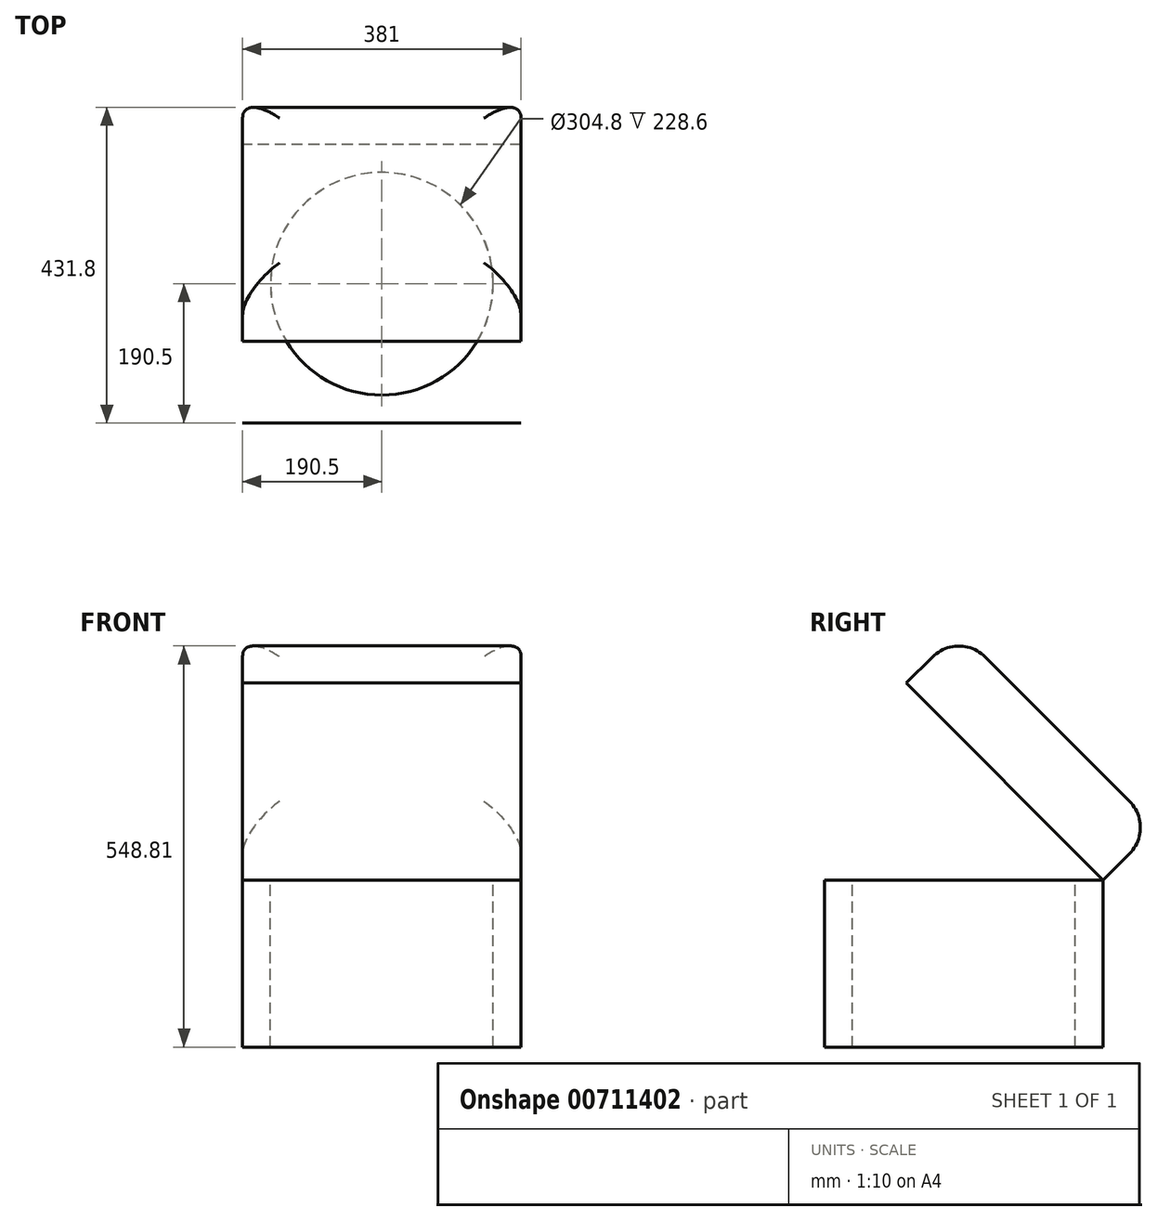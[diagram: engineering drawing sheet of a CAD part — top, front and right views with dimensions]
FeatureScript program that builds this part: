
annotation { "Feature Type Name" : "Feature", "Feature Type Description" : "" }
export const myFeature = defineFeature(function(context is Context, id is Id, definition is map)
    precondition{}
    {
        {
            var Q0;
            Q0=qCreatedBy(makeId("Top.planeOp"),FACE);
            var sketch = newSketch(context, id + "F0", { "sketchPlane" : qUnion([Q0])});
            skLineSegment(sketch, "E0.bottom", {"start": v(190.5, -190.5) * mm, "end": v(-190.5, -190.5) * mm});
            skLineSegment(sketch, "E0.top", {"start": v(190.5, 190.5) * mm, "end": v(-190.5, 190.5) * mm});
            skLineSegment(sketch, "E0.left", {"start": v(190.5, -190.5) * mm, "end": v(190.5, 190.5) * mm});
            skLineSegment(sketch, "E0.right", {"start": v(-190.5, -190.5) * mm, "end": v(-190.5, 190.5) * mm});
            skLineSegment(sketch, "E1", {"start": v(-190.5, 190.5) * mm, "end": v(190.5, -190.5) * mm, "construction": true});
            skSolve(sketch);
        }
        {
            var Q0;
            Q0=makeQuery(id+"F0.imprint","IMPRINT",FACE,{"disambiguationData":[TD([[makeQuery(id+"F0.imprint","IMPRINT",EDGE,{"derivedFrom":sQuery(id+"F0.wireOp",EDGE,"E0.bottom")}),-1.0]])]});
            extrude(context, id + "F1", {"entities" : qUnion([Q0]), "oppositeDirection" : true, "depth" : 228.6 * mm, "offsetDistance" : 25.4 * mm});
        }
        {
            var Q0;
            Q0=makeQuery(id+"F1.opExtrude","CAP_FACE",FACE,{"disambiguationData":[OSD([sQuery(id+"F0.wireOp",EDGE,"E0.bottom"),sQuery(id+"F0.wireOp",EDGE,"E0.top"),sQuery(id+"F0.wireOp",EDGE,"E0.left"),sQuery(id+"F0.wireOp",EDGE,"E0.right")])],"isStart":true});
            var Q1;
            Q1=makeQuery(id+"F1.opExtrude","CAP_EDGE",EDGE,{"disambiguationData":[OSD([sQuery(id+"F0.wireOp",EDGE,"E0.top")])],"isStart":true});
            cPlane(context, id + "F2", {"entities" : qUnion([Q0, Q1]), "cplaneType" : CPlaneType.LINE_ANGLE, "offset" : 25.4 * mm, "angle" : 45 * degree, "width" : 152.4 * mm, "height" : 152.4 * mm});
        }
        {
            var Q0;
            Q0=qCreatedBy(makeId("Right.planeOp"),FACE);
            var sketch = newSketch(context, id + "F3", { "sketchPlane" : qUnion([Q0])});
            skLineSegment(sketch, "E2.0", {"start": v(-190.5, 0) * mm, "end": v(190.5, 0) * mm, "construction": true});
            skLineSegment(sketch, "E3", {"start": v(190.5, 0) * mm, "end": v(-78.9, 269.4) * mm});
            skLineSegment(sketch, "E4", {"start": v(-78.9, 269.4) * mm, "end": v(-7.07, 341.25) * mm});
            skLineSegment(sketch, "E5", {"start": v(-7.07, 341.25) * mm, "end": v(262.34, 71.84) * mm});
            skLineSegment(sketch, "E6", {"start": v(262.34, 71.84) * mm, "end": v(190.5, 0) * mm});
            skSolve(sketch);
        }
        {
            var Q0;
            Q0=makeQuery(id+"F3.imprint","IMPRINT",FACE,{"disambiguationData":[TD([[makeQuery(id+"F3.imprint","IMPRINT",EDGE,{"derivedFrom":sQuery(id+"F3.wireOp",EDGE,"E3")}),-1.0]])]});
            extrude(context, id + "F4", {"entities" : qUnion([Q0]), "endBound" : BoundingType.SYMMETRIC, "depth" : 381 * mm, "offsetDistance" : 25.4 * mm});
        }
        {
            var Q0;
            Q0=makeQuery(id+"F4.opExtrude","SWEPT_FACE",FACE,{"disambiguationData":[OSD([sQuery(id+"F3.wireOp",EDGE,"E5")])]});
            fillet(context, id + "F5", {"entities" : qUnion([Q0]), "radius" : 50.8 * mm, "tangentPropagation" : true, "allowEdgeOverflow" : false});
        }
        {
            var Q0;
            Q0=makeQuery(id+"F1.opExtrude","CAP_FACE",FACE,{"disambiguationData":[OSD([sQuery(id+"F0.wireOp",EDGE,"E0.bottom"),sQuery(id+"F0.wireOp",EDGE,"E0.top"),sQuery(id+"F0.wireOp",EDGE,"E0.left"),sQuery(id+"F0.wireOp",EDGE,"E0.right")])],"isStart":true});
            var sketch = newSketch(context, id + "F6", { "sketchPlane" : qUnion([Q0])});
            skCircle(sketch, "E7", {"center": v(0, 0) * mm, "radius": 152.4 * mm});
            skSolve(sketch);
        }
        {
            var Q0;
            Q0=makeQuery(id+"F6.imprint","IMPRINT",FACE,{"disambiguationData":[TD([[makeQuery(id+"F6.imprint","IMPRINT",EDGE,{"derivedFrom":sQuery(id+"F6.wireOp",EDGE,"E7")}),1.0]])]});
            extrude(context, id + "F7", {"entities" : qUnion([Q0]), "operationType" : NewBodyOperationType.REMOVE, "endBound" : BoundingType.THROUGH_ALL, "oppositeDirection" : true, "depth" : 25.4 * mm, "offsetDistance" : 25.4 * mm});
        }
    });
